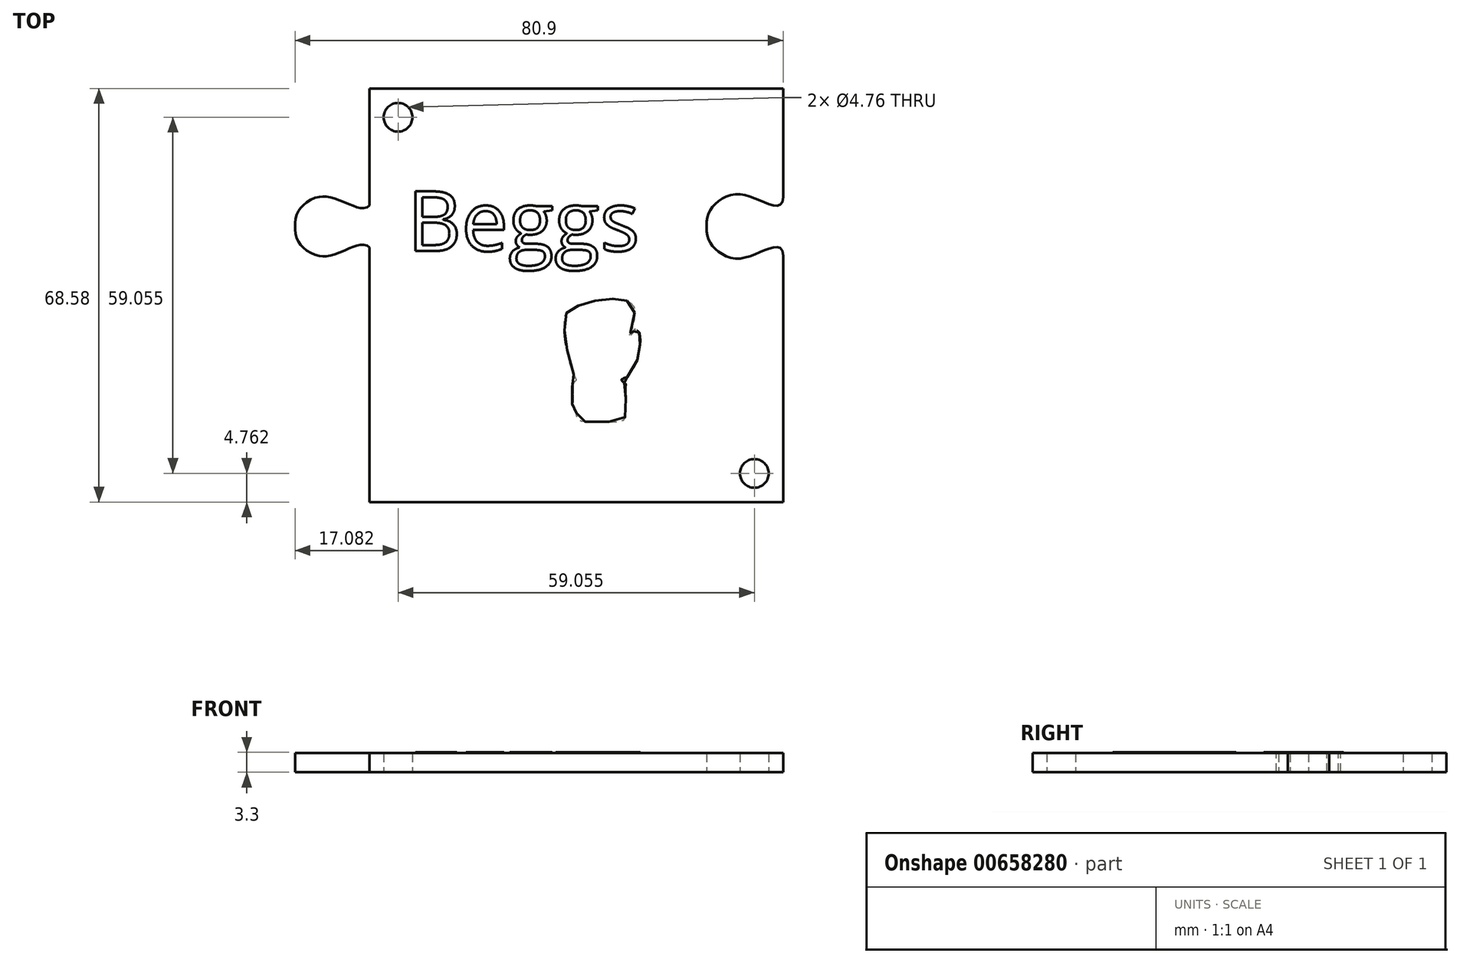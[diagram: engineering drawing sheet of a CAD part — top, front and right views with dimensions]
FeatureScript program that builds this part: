
annotation { "Feature Type Name" : "Feature", "Feature Type Description" : "" }
export const myFeature = defineFeature(function(context is Context, id is Id, definition is map)
    precondition{}
    {
        {
            var Q0;
            Q0=qCreatedBy(makeId("Top.planeOp"),FACE);
            var sketch = newSketch(context, id + "F0", { "sketchPlane" : qUnion([Q0])});
            skLineSegment(sketch, "E0.bottom", {"start": v(34.3, 34.3) * mm, "end": v(-34.3, 34.3) * mm});
            skLineSegment(sketch, "E0.top", {"start": v(34.3, -34.3) * mm, "end": v(-34.3, -34.3) * mm});
            skLineSegment(sketch, "E0.left", {"start": v(34.3, 34.3) * mm, "end": v(34.3, -34.3) * mm});
            skLineSegment(sketch, "E0.right", {"start": v(-34.3, 34.3) * mm, "end": v(-34.3, -34.3) * mm});
            skPoint(sketch, "E0.middle", {"position": v(0, 0) * mm});
            skCircle(sketch, "E1", {"center": v(-29.53, 29.53) * mm, "radius": 2.38 * mm});
            skCircle(sketch, "E2.MirrorC", {"center": v(29.53, -29.53) * mm, "radius": 2.38 * mm});
            skSolve(sketch);
        }
        {
            var Q0;
            Q0=qSketchRegion(id+"F0",true);
            extrude(context, id + "F1", {"entities" : qUnion([Q0]), "depth" : 3.17 * mm});
        }
        {
            var Q0;
            Q0=qCreatedBy(makeId("Top.planeOp"),FACE);
            var sketch = newSketch(context, id + "F2", { "sketchPlane" : qUnion([Q0])});
            skPoint(sketch, "E3", {"position": v(-34.3, 16.33) * mm});
            skPoint(sketch, "E4", {"position": v(-36.2, 14.99) * mm});
            skPoint(sketch, "E5", {"position": v(-41.66, 16.76) * mm});
            skPoint(sketch, "E6", {"position": v(-45.72, 14.99) * mm});
            skPoint(sketch, "E7", {"position": v(-47, 11.43) * mm});
            skFitSpline(sketch, "E8", {"points": [v(-34.3, 16.33) * mm, v(-36.2, 14.99) * mm, v(-41.66, 16.76) * mm, v(-45.72, 14.99) * mm, v(-47, 11.43) * mm], "startDerivative": vector(0, -24.54) * mm, "endDerivative": vector(0, -20.15) * mm});
            skLineSegment(sketch, "E9", {"start": v(-47, 11.43) * mm, "end": v(-29.95, 11.43) * mm, "construction": true});
            skFitSpline(sketch, "E10.MirrorCS", {"points": [v(-34.3, 6.53) * mm, v(-36.2, 7.87) * mm, v(-41.66, 6.1) * mm, v(-45.72, 7.87) * mm, v(-47, 11.43) * mm], "startDerivative": vector(0, 24.54) * mm, "endDerivative": vector(0, 20.15) * mm});
            skLineSegment(sketch, "E11", {"start": v(-34.3, 16.33) * mm, "end": v(-34.3, 6.53) * mm, "construction": true});
            skFitSpline(sketch, "E12.MirrorCS", {"points": [v(-34.3, 16.33) * mm, v(-32.39, 14.99) * mm, v(-26.92, 16.76) * mm, v(-22.86, 14.99) * mm, v(-21.59, 11.43) * mm], "startDerivative": vector(0, -24.54) * mm, "endDerivative": vector(0, -20.15) * mm});
            skFitSpline(sketch, "E13.MirrorCS", {"points": [v(-34.3, 6.53) * mm, v(-32.39, 7.87) * mm, v(-26.92, 6.1) * mm, v(-22.86, 7.87) * mm, v(-21.59, 11.43) * mm], "startDerivative": vector(0, 24.54) * mm, "endDerivative": vector(0, 20.15) * mm});
            skFitSpline(sketch, "E14.0", {"points": [v(-33.9, 6.53) * mm, v(-33.9, 6.8) * mm, v(-33.96, 7.3) * mm, v(-34.16, 7.77) * mm, v(-34.42, 8.07) * mm, v(-34.73, 8.28) * mm, v(-35.16, 8.4) * mm, v(-35.7, 8.38) * mm, v(-36.22, 8.27) * mm, v(-36.76, 8.1) * mm, v(-37.5, 7.83) * mm, v(-38.44, 7.42) * mm, v(-39.6, 6.94) * mm, v(-40.54, 6.64) * mm, v(-41.28, 6.5) * mm, v(-41.8, 6.46) * mm, v(-42.32, 6.5) * mm, v(-43, 6.62) * mm, v(-43.8, 6.91) * mm, v(-44.68, 7.44) * mm, v(-45.29, 7.96) * mm, v(-45.69, 8.4) * mm, v(-46.02, 8.85) * mm, v(-46.33, 9.45) * mm, v(-46.56, 10.3) * mm, v(-46.6, 11.03) * mm, v(-46.6, 11.43) * mm]});
            skFitSpline(sketch, "E14.1", {"points": [v(-33.9, 16.33) * mm, v(-33.9, 16.05) * mm, v(-33.96, 15.56) * mm, v(-34.16, 15.09) * mm, v(-34.42, 14.8) * mm, v(-34.73, 14.58) * mm, v(-35.16, 14.46) * mm, v(-35.7, 14.48) * mm, v(-36.22, 14.6) * mm, v(-36.76, 14.76) * mm, v(-37.5, 15.03) * mm, v(-38.44, 15.44) * mm, v(-39.6, 15.92) * mm, v(-40.54, 16.22) * mm, v(-41.28, 16.36) * mm, v(-41.8, 16.4) * mm, v(-42.32, 16.37) * mm, v(-43, 16.24) * mm, v(-43.8, 15.95) * mm, v(-44.68, 15.42) * mm, v(-45.29, 14.9) * mm, v(-45.69, 14.46) * mm, v(-46.02, 14.01) * mm, v(-46.33, 13.41) * mm, v(-46.56, 12.55) * mm, v(-46.6, 11.83) * mm, v(-46.6, 11.43) * mm]});
            skLineSegment(sketch, "E15", {"start": v(-34.3, 16.33) * mm, "end": v(-34.3, 6.53) * mm});
            skLineSegment(sketch, "E16", {"start": v(-34.3, 7.92) * mm, "end": v(-34.3, 14.94) * mm});
            skFitSpline(sketch, "E17.MirrorCS", {"points": [v(34.3, 16.33) * mm, v(32.39, 14.99) * mm, v(26.92, 16.76) * mm, v(22.86, 14.99) * mm, v(21.59, 11.43) * mm], "startDerivative": vector(0, -24.54) * mm, "endDerivative": vector(0, -20.15) * mm});
            skFitSpline(sketch, "E18.MirrorCS", {"points": [v(34.3, 6.53) * mm, v(32.39, 7.87) * mm, v(26.92, 6.1) * mm, v(22.86, 7.87) * mm, v(21.59, 11.43) * mm], "startDerivative": vector(0, 24.54) * mm, "endDerivative": vector(0, 20.15) * mm});
            skLineSegment(sketch, "E19", {"start": v(34.3, 16.33) * mm, "end": v(39.12, 16.33) * mm});
            skLineSegment(sketch, "E20", {"start": v(39.12, 16.33) * mm, "end": v(39.12, 6.53) * mm});
            skLineSegment(sketch, "E21", {"start": v(39.12, 6.53) * mm, "end": v(34.3, 6.53) * mm});
            skSolve(sketch);
        }
        {
            var Q0;
            Q0=makeQuery(id+"F2.imprint","IMPRINT",FACE,{"disambiguationData":[TD([[makeQuery(id+"F2.imprint","IMPRINT",EDGE,{"derivedFrom":sQuery(id+"F2.wireOp",EDGE,"E14.0")}),-1.0]])]});
            var Q1;
            Q1=makeQuery(id+"F1.opExtrude","CAP_FACE",FACE,{"disambiguationData":[OSD([sQuery(id+"F0.wireOp",EDGE,"E0.bottom"),sQuery(id+"F0.wireOp",EDGE,"E0.top"),sQuery(id+"F0.wireOp",EDGE,"E0.left"),sQuery(id+"F0.wireOp",EDGE,"E0.right"),sQuery(id+"F0.wireOp",EDGE,"E1"),sQuery(id+"F0.wireOp",EDGE,"e1648c08-8adf-473f-9b64-c467cf328ef90.MirrorC"),sQuery(id+"F0.wireOp",EDGE,"1cdcda55-2210-49d8-b5f0-9198a802923b0.MirrorC"),sQuery(id+"F0.wireOp",EDGE,"E2.MirrorC")])],"isStart":false});
            extrude(context, id + "F3", {"entities" : qUnion([Q0]), "operationType" : NewBodyOperationType.ADD, "endBound" : BoundingType.UP_TO_SURFACE, "endBoundEntityFace" : qUnion([Q1]), "depth" : 25.4 * mm});
        }
        {
            var Q0;
            Q0=qCreatedBy(makeId("Right.planeOp"),FACE);
            var sketch = newSketch(context, id + "F4", { "sketchPlane" : qUnion([Q0])});
            skLineSegment(sketch, "E22", {"start": v(0, -65.87) * mm, "end": v(0, 47.63) * mm});
            skSolve(sketch);
        }
        {
            var Q0;
            Q0=makeQuery(id+"F2.imprint","IMPRINT",FACE,{"disambiguationData":[TD([[makeQuery(id+"F2.imprint","IMPRINT",EDGE,{"derivedFrom":sQuery(id+"F2.wireOp",EDGE,"E17.MirrorCS")}),1.0]])]});
            extrude(context, id + "F5", {"entities" : qUnion([Q0]), "operationType" : NewBodyOperationType.REMOVE, "endBound" : BoundingType.THROUGH_ALL, "depth" : 25.4 * mm});
        }
        {
            var Q0;
            {var subQ0=sQuery(id+"F0.wireOp",EDGE,"E2.MirrorC");var subQ1=sQuery(id+"F0.wireOp",EDGE,"E1");var subQ2=sQuery(id+"F0.wireOp",EDGE,"E0.right");var subQ3=sQuery(id+"F0.wireOp",EDGE,"E0.left");var subQ4=sQuery(id+"F0.wireOp",EDGE,"E0.top");var subQ5=sQuery(id+"F0.wireOp",EDGE,"E0.bottom");Q0=makeQuery(id+"FDfX84p6046V9zH_1.3.F3.boolean.opBoolean","MERGE",FACE,{"derivedFrom":[makeQuery(id+"FDfX84p6046V9zH_1.2.F3.boolean.opBoolean","MERGE",FACE,{"derivedFrom":[makeQuery(id+"FDfX84p6046V9zH_1.1.F3.boolean.opBoolean","MERGE",FACE,{"derivedFrom":[makeQuery(id+"F3.boolean.opBoolean","MERGE",FACE,{"derivedFrom":[makeQuery(id+"F1.opExtrude","CAP_FACE",FACE,{"disambiguationData":[OSD([subQ5,subQ4,subQ3,subQ2,subQ1,subQ0])],"isStart":false}),makeQuery(id+"F3.opExtrude","CAP_FACE",FACE,{"disambiguationData":[OSD([subQ5,subQ4,subQ3,subQ2,subQ1,subQ0])],"isStart":false})]}),makeQuery(id+"FDfX84p6046V9zH_1.1.F3.opExtrude","CAP_FACE",FACE,{"disambiguationData":[OSD([subQ5,subQ4,subQ3,subQ2,subQ1,subQ0])],"isStart":false})]}),makeQuery(id+"FDfX84p6046V9zH_1.2.F3.opExtrude","CAP_FACE",FACE,{"disambiguationData":[OSD([subQ5,subQ4,subQ3,subQ2,subQ1,subQ0])],"isStart":false})]}),makeQuery(id+"FDfX84p6046V9zH_1.3.F3.opExtrude","CAP_FACE",FACE,{"disambiguationData":[OSD([subQ5,subQ4,subQ3,subQ2,subQ1,subQ0])],"isStart":false})]});}
            var sketch = newSketch(context, id + "F6", { "sketchPlane" : qUnion([Q0])});
            skText(sketch, "E23", { "text": "Beggs", "fontName": "OpenSans-Regular.ttf"});
            const initialGuessF6  = {"E23": [-0.028, 0.00736, 1, 0, 0.00997]};
            skSetInitialGuess(sketch, initialGuessF6);
            skSolve(sketch);
        }
        {
            var Q0;
            Q0=makeQuery(id+"F6.imprint","IMPRINT",FACE,{"disambiguationData":[TD([[makeQuery(id+"F6.imprint","IMPRINT",EDGE,{"derivedFrom":sQuery(id+"F6.wireOp",EDGE,"E23.sketch_text.stroke-0")}),1.0]])]});
            var sketch = newSketch(context, id + "F7", { "sketchPlane" : qUnion([Q0])});
            skFitSpline(sketch, "E24", {"points": [v(-1.94, -5.78) * mm, v(-1.94, -4.07) * mm, v(-1.62, -2.95) * mm, v(-0.83, -2.3) * mm, v(0, -1.86) * mm, v(0.54, -1.63) * mm, v(1.77, -1.24) * mm, v(3.58, -0.77) * mm, v(4.85, -0.61) * mm, v(6.43, -0.56) * mm, v(7.2, -0.68) * mm, v(8, -0.75) * mm, v(9.24, -1.4) * mm, v(9.59, -1.98) * mm, v(9.66, -3.42) * mm, v(9.29, -5.41) * mm, v(8.7, -6.85) * mm, v(8.66, -6.97) * mm, v(9.08, -6.64) * mm, v(9.68, -5.67) * mm, v(9.7, -5.5) * mm, v(10.05, -5.8) * mm, v(10.26, -5.95) * mm, v(10.47, -6.25) * mm, v(10.54, -6.64) * mm, v(10.6, -7.22) * mm, v(10.54, -8.43) * mm, v(10.38, -9.64) * mm, v(10.17, -10.59) * mm, v(9.38, -12.33) * mm, v(8.4, -13.56) * mm, v(8.15, -13.67) * mm, v(7.52, -13.97) * mm, v(7.55, -14.16) * mm, v(8.15, -14.67) * mm, v(8.16, -15.16) * mm, v(8.21, -17.23) * mm, v(8.18, -19.3) * mm, v(8.1, -20.25) * mm, v(7.57, -20.86) * mm, v(5.53, -20.99) * mm, v(3.13, -20.9) * mm, v(0.67, -20.85) * mm, v(0.2, -20.37) * mm, v(0, -19.53) * mm, v(0, -19.26) * mm, v(-0.28, -19.07) * mm, v(-0.59, -18.57) * mm, v(-0.63, -17.41) * mm, v(-0.65, -15.22) * mm, v(-0.46, -14.47) * mm, v(0, -14.07) * mm, v(0, -13.9) * mm, v(-0.57, -12.7) * mm, v(-1.38, -9.73) * mm, v(-1.8, -7.45) * mm, v(-1.94, -5.78) * mm]});
            skSolve(sketch);
        }
        {
            var Q0;
            Q0 = qSketchRegion(id + "F7", true);
            extrude(context, id + "F8", {"entities" : qUnion([Q0]), "operationType" : NewBodyOperationType.ADD, "depth" : 0.13 * mm, "offsetDistance" : 25.4 * mm});
        }
        {
            var Q0;
            Q0 = qSketchRegion(id + "F6", true);
            extrude(context, id + "F9", {"entities" : qUnion([Q0]), "operationType" : NewBodyOperationType.ADD, "depth" : 0.13 * mm, "offsetDistance" : 25.4 * mm});
        }
    });
